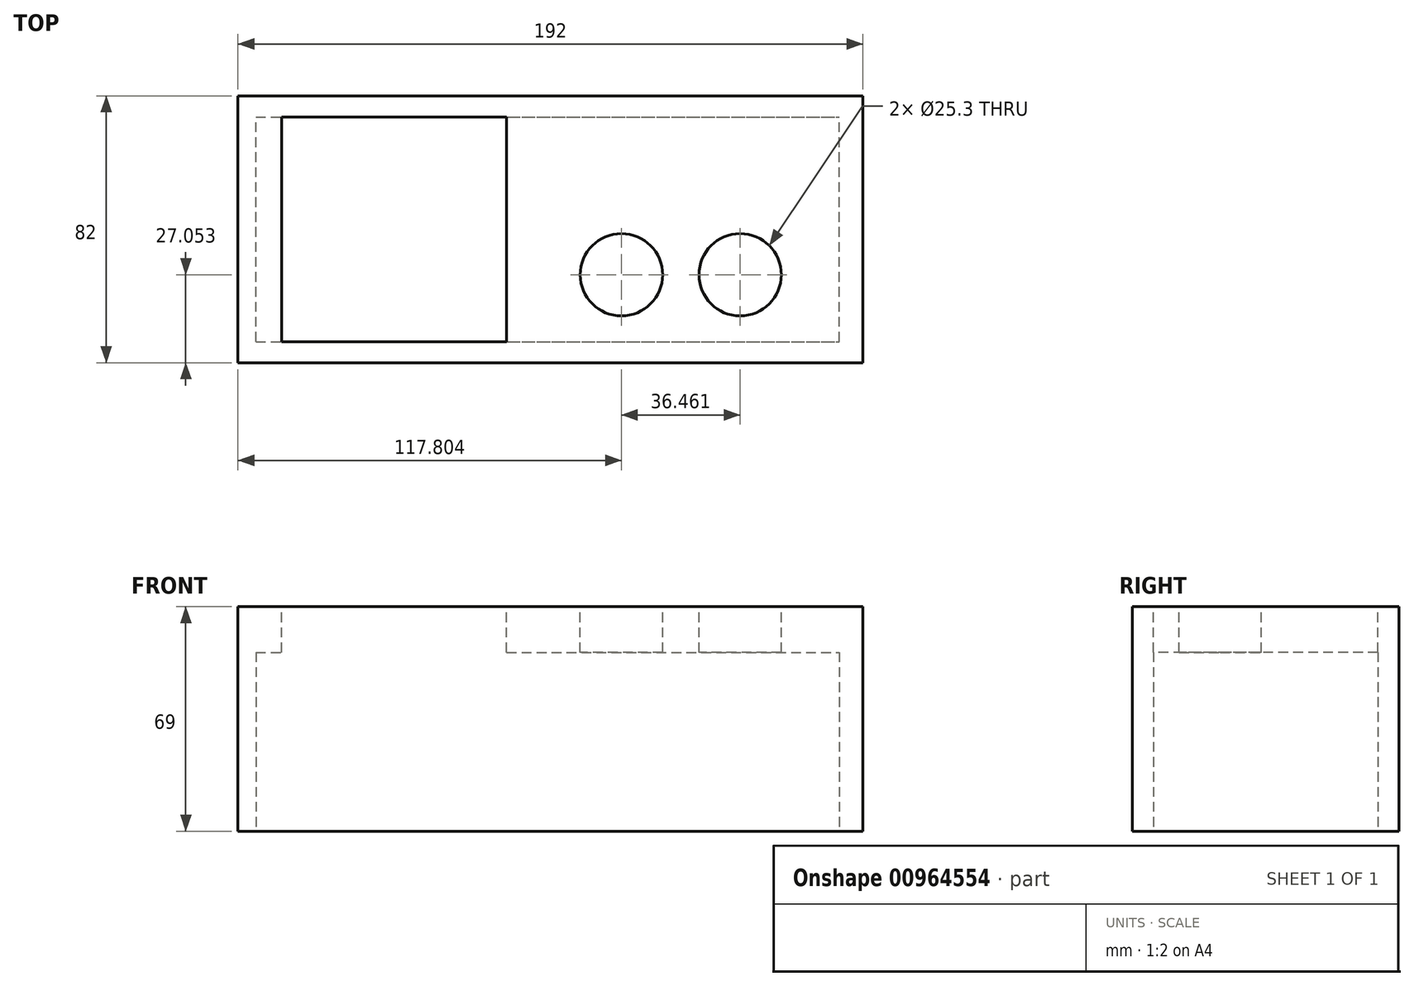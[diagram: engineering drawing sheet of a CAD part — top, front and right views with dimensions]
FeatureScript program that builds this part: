
annotation { "Feature Type Name" : "Feature", "Feature Type Description" : "" }
export const myFeature = defineFeature(function(context is Context, id is Id, definition is map)
    precondition{}
    {
        {
            var Q0;
            Q0=qCreatedBy(makeId("Top.planeOp"),FACE);
            var sketch = newSketch(context, id + "F0", { "sketchPlane" : qUnion([Q0])});
            skLineSegment(sketch, "E0.bottom", {"start": v(-34.55, 34.5) * mm, "end": v(34.55, 34.5) * mm});
            skLineSegment(sketch, "E0.top", {"start": v(-34.55, -34.5) * mm, "end": v(34.55, -34.5) * mm});
            skLineSegment(sketch, "E0.left", {"start": v(-34.55, 34.5) * mm, "end": v(-34.55, -34.5) * mm});
            skLineSegment(sketch, "E0.right", {"start": v(34.55, 34.5) * mm, "end": v(34.55, -34.5) * mm});
            skPoint(sketch, "E0.middle", {"position": v(0, 0) * mm});
            skLineSegment(sketch, "E1.bottom", {"start": v(-48, 41) * mm, "end": v(48, 41) * mm});
            skLineSegment(sketch, "E1.top", {"start": v(-48, -41) * mm, "end": v(48, -41) * mm});
            skLineSegment(sketch, "E1.left", {"start": v(-48, 41) * mm, "end": v(-48, -41) * mm});
            skLineSegment(sketch, "E1.right", {"start": v(48, 41) * mm, "end": v(48, -41) * mm});
            skLineSegment(sketch, "E2.bottom", {"start": v(48, 41) * mm, "end": v(144, 41) * mm});
            skLineSegment(sketch, "E2.top", {"start": v(48, -41) * mm, "end": v(144, -41) * mm});
            skLineSegment(sketch, "E2.right", {"start": v(144, 41) * mm, "end": v(144, -41) * mm});
            skCircle(sketch, "E3", {"center": v(69.8, -13.95) * mm, "radius": 12.65 * mm});
            skCircle(sketch, "E4", {"center": v(106.27, -13.95) * mm, "radius": 12.65 * mm});
            skCircle(sketch, "E5", {"center": v(69.8, -13.95) * mm, "radius": 16.48 * mm});
            skCircle(sketch, "E6", {"center": v(106.27, -13.95) * mm, "radius": 16.48 * mm});
            skSolve(sketch);
        }
        {
            var Q0;
            Q0=makeQuery(id+"F0.imprint","IMPRINT",FACE,{"disambiguationData":[TD([[makeQuery(id+"F0.imprint","IMPRINT",EDGE,{"derivedFrom":sQuery(id+"F0.wireOp",EDGE,"E0.bottom")}),1.0]])]});
            var Q1;
            Q1=makeQuery(id+"F0.imprint","IMPRINT",FACE,{"disambiguationData":[TD([[makeQuery(id+"F0.imprint","IMPRINT",EDGE,{"derivedFrom":sQuery(id+"F0.wireOp",EDGE,"E2.bottom")}),-1.0]])]});
            var Q2;
            Q2=makeQuery(id+"F0.imprint","IMPRINT",FACE,{"disambiguationData":[TD([[makeQuery(id+"F0.imprint","IMPRINT",EDGE,{"derivedFrom":sQuery(id+"F0.wireOp",EDGE,"E3")}),-1.0]])]});
            var Q3;
            Q3=makeQuery(id+"F0.imprint","IMPRINT",FACE,{"disambiguationData":[TD([[makeQuery(id+"F0.imprint","IMPRINT",EDGE,{"derivedFrom":sQuery(id+"F0.wireOp",EDGE,"E4")}),-1.0]])]});
            extrude(context, id + "F1", {"entities" : qUnion([Q0, Q1, Q2, Q3]), "oppositeDirection" : true, "depth" : 69 * mm, "offsetDistance" : 25 * mm});
        }
        {
            var Q0;
            Q0=makeQuery(id+"F1.opExtrude","CAP_FACE",FACE,{"disambiguationData":[OSD([sQuery(id+"F0.wireOp",EDGE,"E0.bottom"),sQuery(id+"F0.wireOp",EDGE,"E0.top"),sQuery(id+"F0.wireOp",EDGE,"E0.left"),sQuery(id+"F0.wireOp",EDGE,"E0.right"),sQuery(id+"F0.wireOp",EDGE,"E1.bottom"),sQuery(id+"F0.wireOp",EDGE,"E1.top"),sQuery(id+"F0.wireOp",EDGE,"E1.left"),sQuery(id+"F0.wireOp",EDGE,"E2.bottom"),sQuery(id+"F0.wireOp",EDGE,"E2.top"),sQuery(id+"F0.wireOp",EDGE,"E2.right"),sQuery(id+"F0.wireOp",EDGE,"E3"),sQuery(id+"F0.wireOp",EDGE,"E4")])],"isStart":false});
            var sketch = newSketch(context, id + "F2", { "sketchPlane" : qUnion([Q0])});
            skLineSegment(sketch, "E7.bottom", {"start": v(-42.48, 34.5) * mm, "end": v(136.67, 34.5) * mm});
            skLineSegment(sketch, "E7.top", {"start": v(-42.48, -34.5) * mm, "end": v(136.67, -34.5) * mm});
            skLineSegment(sketch, "E7.left", {"start": v(-42.48, 34.5) * mm, "end": v(-42.48, -34.5) * mm});
            skLineSegment(sketch, "E7.right", {"start": v(136.67, 34.5) * mm, "end": v(136.67, -34.5) * mm});
            skSolve(sketch);
        }
        {
            var Q0;
            {var subQ2=sQuery(id+"F2.wireOp",EDGE,"E7.left");Q0=makeQuery(id+"F2.imprint","IMPRINT",FACE,{"disambiguationData":[TD([[makeQuery(id+"F2.imprint","IMPRINT",EDGE,{"derivedFrom":subQ2}),1.0]])]});}
            var Q1;
            {var subQ1=makeQuery(id+"F1.opExtrude","CAP_EDGE",EDGE,{"disambiguationData":[OSD([sQuery(id+"F0.wireOp",EDGE,"E0.left")])],"isStart":false});Q1=makeQuery(id+"F2.imprint","IMPRINT",FACE,{"disambiguationData":[TD([[makeQuery(id+"F2.imprint","IMPRINT",EDGE,{"derivedFrom":subQ1}),-1.0]])]});}
            var Q2;
            {var subQ2=sQuery(id+"F2.wireOp",EDGE,"E7.right");Q2=makeQuery(id+"F2.imprint","IMPRINT",FACE,{"disambiguationData":[TD([[makeQuery(id+"F2.imprint","IMPRINT",EDGE,{"derivedFrom":subQ2}),-1.0]])]});}
            extrude(context, id + "F3", {"entities" : qUnion([Q0, Q1, Q2]), "operationType" : NewBodyOperationType.REMOVE, "oppositeDirection" : true, "depth" : 55 * mm, "offsetDistance" : 25 * mm});
        }
    });
